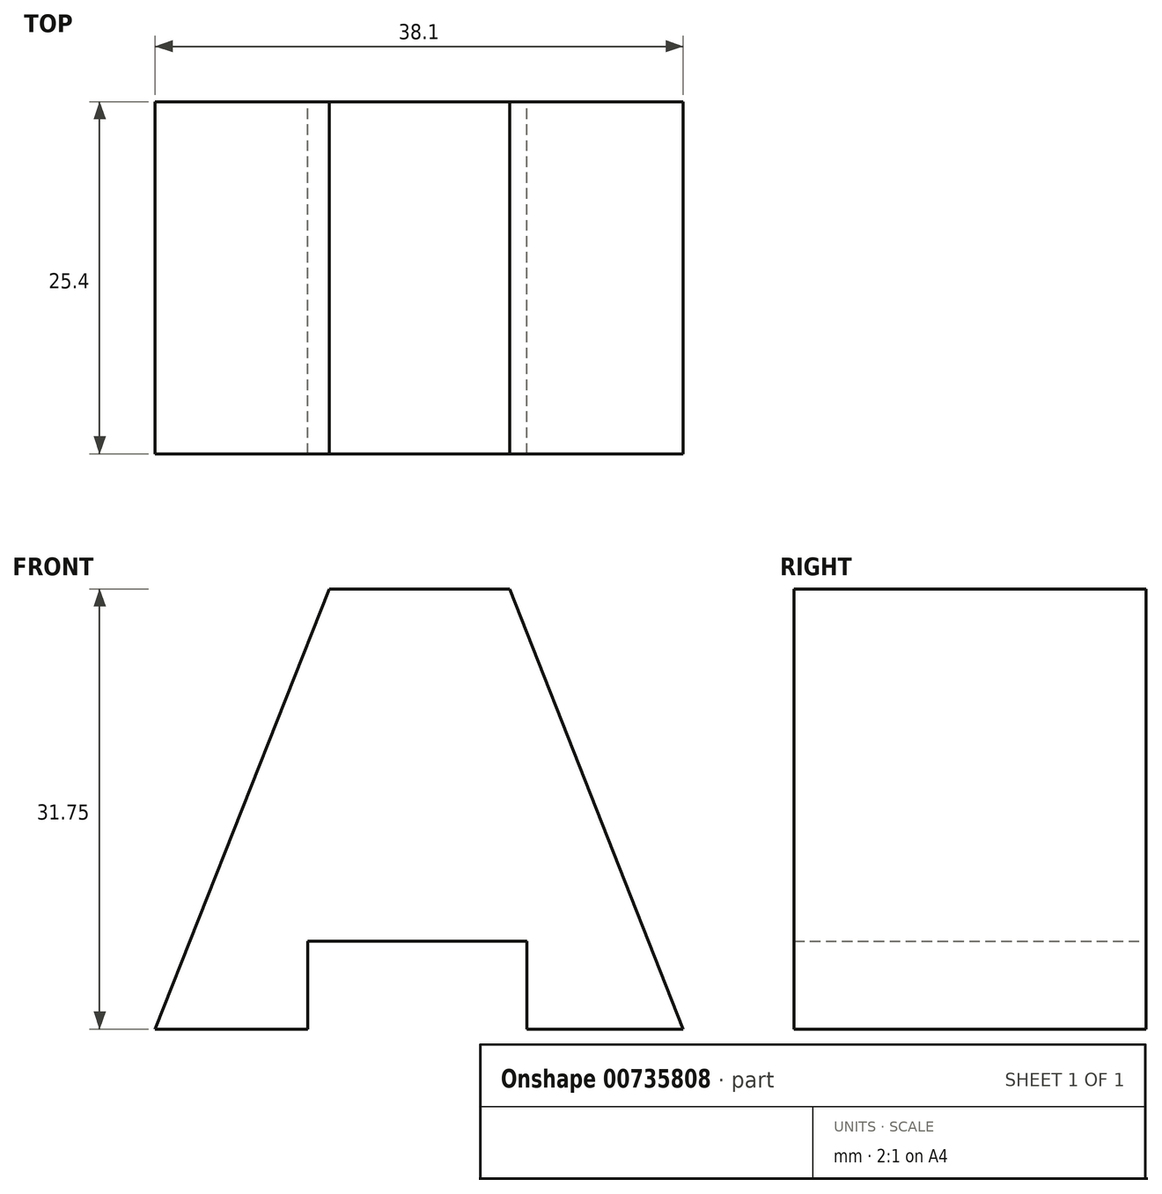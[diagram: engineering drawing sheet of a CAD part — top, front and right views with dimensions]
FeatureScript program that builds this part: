
annotation { "Feature Type Name" : "Feature", "Feature Type Description" : "" }
export const myFeature = defineFeature(function(context is Context, id is Id, definition is map)
    precondition{}
    {
        {
            var Q0;
            Q0=qCreatedBy(makeId("Front.planeOp"),FACE);
            var sketch = newSketch(context, id + "F0", { "sketchPlane" : qUnion([Q0])});
            skLineSegment(sketch, "E0", {"start": v(0, 0) * mm, "end": v(0, 31.75) * mm});
            skLineSegment(sketch, "E1", {"start": v(0, 31.75) * mm, "end": v(38.1, 31.75) * mm});
            skLineSegment(sketch, "E2", {"start": v(38.1, 31.75) * mm, "end": v(38.1, 0) * mm});
            skLineSegment(sketch, "E3", {"start": v(38.1, 0) * mm, "end": v(0, 0) * mm});
            skLineSegment(sketch, "E4", {"start": v(11, 0) * mm, "end": v(11, 6.35) * mm});
            skLineSegment(sketch, "E5", {"start": v(11, 6.35) * mm, "end": v(26.83, 6.35) * mm});
            skLineSegment(sketch, "E6", {"start": v(26.83, 6.35) * mm, "end": v(26.83, 0) * mm});
            skLineSegment(sketch, "E7", {"start": v(25.58, 31.75) * mm, "end": v(38.1, 10.7) * mm});
            skLineSegment(sketch, "E8", {"start": v(12.56, 31.75) * mm, "end": v(0, 11) * mm});
            skLineSegment(sketch, "E9", {"start": v(38.1, 0) * mm, "end": v(25.58, 31.75) * mm});
            skLineSegment(sketch, "E10", {"start": v(0, 0) * mm, "end": v(12.56, 31.75) * mm});
            skSolve(sketch);
        }
        {
            var Q0;
            {var subQ9=sQuery(id+"F0.wireOp",EDGE,"E4");Q0=makeQuery(id+"F0.imprint","IMPRINT",FACE,{"disambiguationData":[TD([[makeQuery(id+"F0.imprint","IMPRINT",EDGE,{"derivedFrom":subQ9}),1.0]])]});}
            extrude(context, id + "F1", {"entities" : qUnion([Q0]), "depth" : 25.4 * mm, "offsetDistance" : 25.4 * mm});
        }
    });
